# Revit family: Astro_ 1163xxx Niimi Round
name_source: partatom
category: Lighting Fixtures
revit_build: Autodesk Revit 2018 (Build: 20170223_1515(x64)
units: mm (PartAtom-declared; Revit-internal decimal feet)

## family parameters
Always vertical = Yes
Cut with Voids When Loaded = No
Host = Wall
Light Source = Yes
OmniClass Number = 23.80.70.00
OmniClass Title = Lighting
Part Type = Normal
Room Calculation Point = No
Round Connector Dimension = Use Diameter
Shared = No

## types (2) — shared parameters
ADA compliant = N / A
Color Filter = 16777215
Dimmable = No
Dimming Lamp Color Temperature Shift = <None>
Driver Included = yes
Driver Required = No
Efficacy (lm/w) = 15
Electrical Class = 2
Emit from Line Length = 610 mm
Lamp = LED
Light Source Fixed = yes
Location / IP Rating = IP44
Main Material = Metal - Steel/Zinc
Manufacturer = Astro Lighting Ltd
Manufacturer URL - Europe and Rest of World = www.astrolighting.com
Manufacturer URL - North America = us.astrolighting.com
Photometric Web File = 1163003_Niimi Round LED_Photometry_IES_Iss. 01.ies
Power (Watts) = 8.3 W
Product CCT = 3000K
Product CRI = 80
Product Dimensions (MM) = 115-350 Projection, 350 Diameter
Product Location = Zone 2, 3
Product Name = Niimi Round LED
Product URL = https://www.astrolighting.com
Product Weight (KG) = 1.95
Tilt Angle = 60.00°
URL = www.astrolighting.com

## per-type parameters (varying)
| type | Main Finish | Product SKU |
| Niimi Round LED Matt Nickel | Matt Nickel | 1163003 |
| Niimi Round LED Polished Chrome | Polished Chrome | 1163001 |

## geometry (parser evidence)
native form markers: Sweep x2
no freeform markers — native parametric forms only
